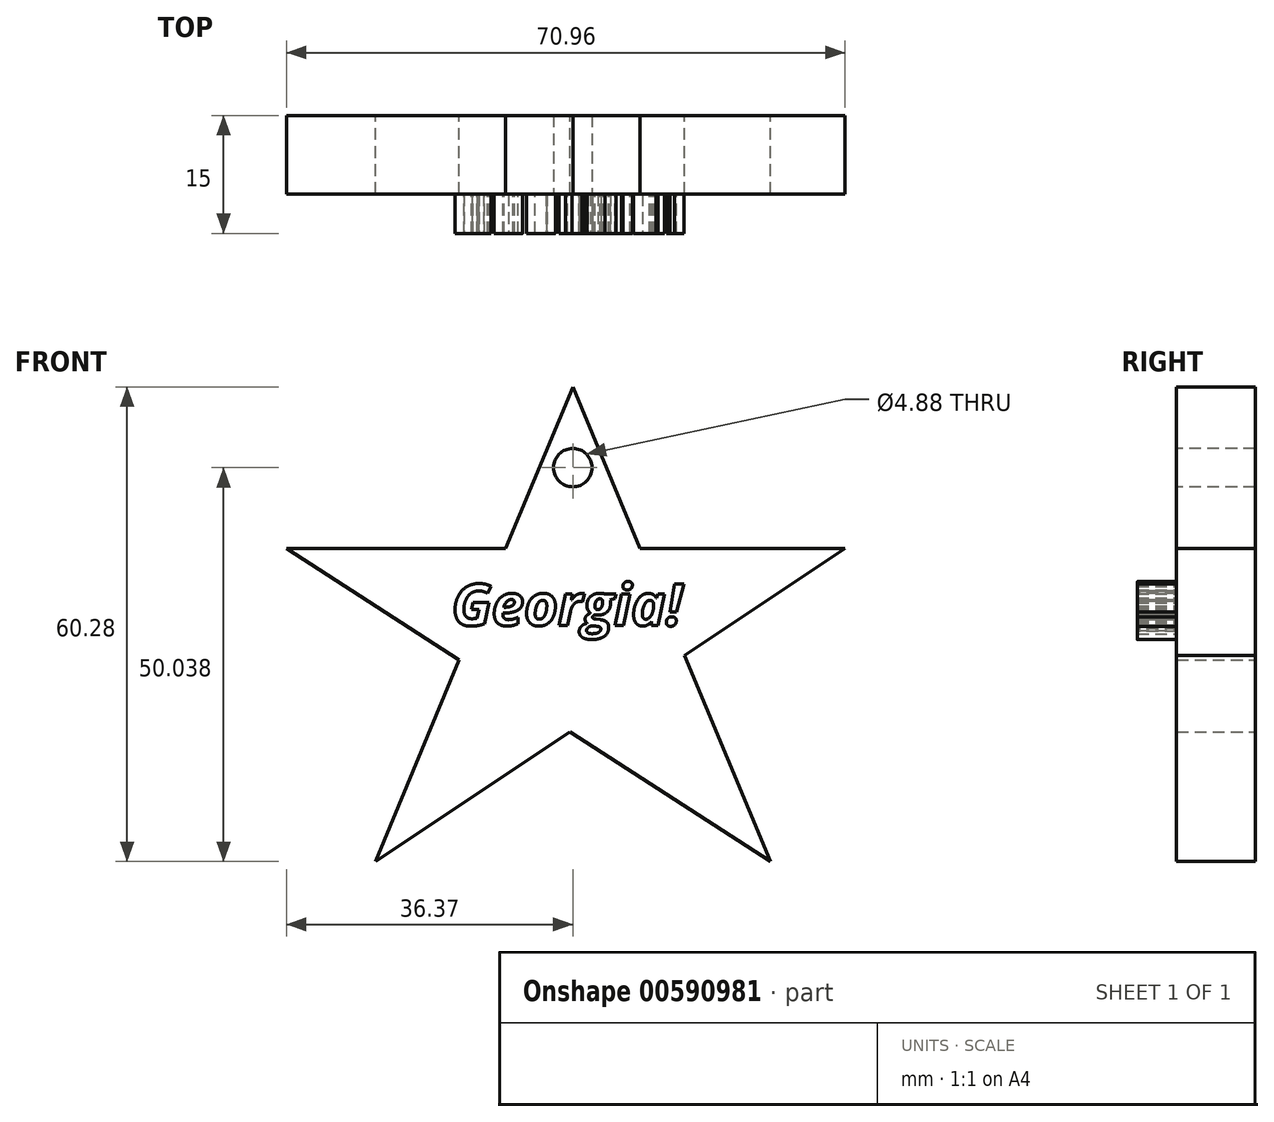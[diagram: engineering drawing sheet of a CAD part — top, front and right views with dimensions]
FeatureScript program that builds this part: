
annotation { "Feature Type Name" : "Feature", "Feature Type Description" : "" }
export const myFeature = defineFeature(function(context is Context, id is Id, definition is map)
    precondition{}
    {
        {
            var Q0;
            Q0=qCreatedBy(makeId("Front.planeOp"),FACE);
            var sketch = newSketch(context, id + "F0", { "sketchPlane" : qUnion([Q0])});
            skLineSegment(sketch, "E0", {"start": v(-25.1, -12.03) * mm, "end": v(-14.44, 13.56) * mm});
            skLineSegment(sketch, "E1.MirrorCS", {"start": v(25.1, -12.03) * mm, "end": v(14.2, 14.16) * mm});
            skLineSegment(sketch, "E2", {"start": v(25.1, -12.03) * mm, "end": v(-0.37, 4.46) * mm});
            skLineSegment(sketch, "E3", {"start": v(-36.37, 27.76) * mm, "end": v(-8.53, 27.76) * mm});
            skLineSegment(sketch, "E4", {"start": v(34.6, 27.76) * mm, "end": v(14.2, 14.16) * mm});
            skLineSegment(sketch, "E5.trimOffspring", {"start": v(-8.53, 27.76) * mm, "end": v(0, 48.25) * mm});
            skLineSegment(sketch, "E6.trimOffspring", {"start": v(-14.44, 13.56) * mm, "end": v(-36.37, 27.76) * mm});
            skLineSegment(sketch, "E7.trimOffspring", {"start": v(-0.37, 4.46) * mm, "end": v(-25.1, -12.03) * mm});
            skLineSegment(sketch, "E8.trimOffspring", {"start": v(8.53, 27.76) * mm, "end": v(0, 48.25) * mm});
            skLineSegment(sketch, "E9.trimOffspring", {"start": v(8.53, 27.76) * mm, "end": v(34.6, 27.76) * mm});
            skSolve(sketch);
        }
        {
            var Q0;
            Q0=makeQuery(id+"F0.imprint","IMPRINT",FACE,{"disambiguationData":[TD([[makeQuery(id+"F0.imprint","IMPRINT",EDGE,{"derivedFrom":sQuery(id+"F0.wireOp",EDGE,"E0")}),-1.0]])]});
            extrude(context, id + "F1", {"entities" : qUnion([Q0]), "depth" : 10 * mm, "offsetDistance" : 25.4 * mm});
        }
        {
            var Q0;
            Q0=makeQuery(id+"F1.opExtrude","CAP_FACE",FACE,{"disambiguationData":[OSD([sQuery(id+"F0.wireOp",EDGE,"E0"),sQuery(id+"F0.wireOp",EDGE,"E1.MirrorCS"),sQuery(id+"F0.wireOp",EDGE,"E2"),sQuery(id+"F0.wireOp",EDGE,"E3"),sQuery(id+"F0.wireOp",EDGE,"E4"),sQuery(id+"F0.wireOp",EDGE,"E5.trimOffspring"),sQuery(id+"F0.wireOp",EDGE,"E6.trimOffspring"),sQuery(id+"F0.wireOp",EDGE,"E7.trimOffspring"),sQuery(id+"F0.wireOp",EDGE,"E8.trimOffspring"),sQuery(id+"F0.wireOp",EDGE,"E9.trimOffspring")])],"isStart":false});
            var sketch = newSketch(context, id + "F2", { "sketchPlane" : qUnion([Q0])});
            skText(sketch, "E10", { "text": "Georgia!", "fontName": "OpenSans-BoldItalic.ttf"});
            const initialGuessF2  = {"E10": [-0.0154, 0.01794, 1, 0, 0.00531]};
            skSetInitialGuess(sketch, initialGuessF2);
            skSolve(sketch);
        }
        {
            var Q0;
            Q0 = qSketchRegion(id + "F2", true);
            extrude(context, id + "F3", {"entities" : qUnion([Q0]), "operationType" : NewBodyOperationType.ADD, "depth" : 5 * mm, "offsetDistance" : 25 * mm});
        }
        {
            var Q0;
            {var subQ0=sQuery(id+"F0.wireOp",EDGE,"E9.trimOffspring");var subQ1=sQuery(id+"F0.wireOp",EDGE,"E8.trimOffspring");var subQ2=sQuery(id+"F0.wireOp",EDGE,"E7.trimOffspring");var subQ3=sQuery(id+"F0.wireOp",EDGE,"E4");var subQ4=sQuery(id+"F0.wireOp",EDGE,"E2");var subQ5=sQuery(id+"F0.wireOp",EDGE,"E1.MirrorCS");var subQ6=sQuery(id+"F0.wireOp",EDGE,"E3");var subQ7=sQuery(id+"F0.wireOp",EDGE,"E0");var subQ8=sQuery(id+"F0.wireOp",EDGE,"E5.trimOffspring");var subQ9=sQuery(id+"F0.wireOp",EDGE,"E6.trimOffspring");Q0=makeQuery(id+"F3.boolean.opBoolean","SPLIT",FACE,{"disambiguationData":[TD([makeQuery(id+"F1.opExtrude","SWEPT_FACE",FACE,{"disambiguationData":[OSD([subQ7])]})])],"derivedFrom":makeQuery(id+"F1.opExtrude","CAP_FACE",FACE,{"disambiguationData":[OSD([subQ7,subQ5,subQ4,subQ6,subQ3,subQ8,subQ9,subQ2,subQ1,subQ0])],"isStart":false})});}
            var sketch = newSketch(context, id + "F4", { "sketchPlane" : qUnion([Q0])});
            skCircle(sketch, "E11", {"center": v(0, 38) * mm, "radius": 2.44 * mm});
            skPoint(sketch, "E11.centerSnap0", {"position": v(4.26, 38) * mm});
            skSolve(sketch);
        }
        {
            var Q0;
            Q0=makeQuery(id+"F4.imprint","IMPRINT",FACE,{"disambiguationData":[TD([[makeQuery(id+"F4.imprint","IMPRINT",EDGE,{"derivedFrom":sQuery(id+"F4.wireOp",EDGE,"E11")}),1.0]])]});
            extrude(context, id + "F5", {"entities" : qUnion([Q0]), "operationType" : NewBodyOperationType.REMOVE, "endBound" : BoundingType.THROUGH_ALL, "oppositeDirection" : true, "depth" : 30 * mm, "offsetDistance" : 25 * mm});
        }
    });
